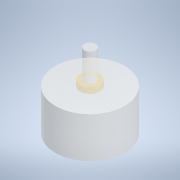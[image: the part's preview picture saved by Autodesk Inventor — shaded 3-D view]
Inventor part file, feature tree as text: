
AUTODESK INVENTOR PART (.ipt)
format: ipt  version: 2020 (Build 240168000, 168)  size: 116,224 bytes
history: native  units: mm
features: extrude x3, sketch x3, other x2
ambient origin geometry x8: Origin, YZ Plane, XZ Plane, XY Plane, X Axis, Y Axis, Z Axis, Center Point
bodies: Body1 (feature_tree), Body2 (feature_tree)
feature tree (8):
  other  "Bryła1"
  extrude  "Wyciągnięcie proste1"  Depth=24.7mm
  extrude  "Wyciągnięcie proste2"  Depth=14.5mm TaperAngle=0.0deg
  extrude  "Wyciągnięcie proste3"  Depth=7.0mm
  sketch  "Szkic1"
  sketch  "Szkic2"
  other  "Bryła2"
  sketch  "Szkic3"
